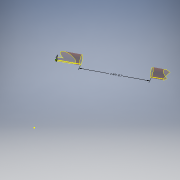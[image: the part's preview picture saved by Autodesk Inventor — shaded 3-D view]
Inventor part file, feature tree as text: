
AUTODESK INVENTOR PART (.ipt)
format: ipt  version: 2019.3 (Build 233278000, 278)  size: 225,280 bytes
history: native  units: mm
features: other x5, sketch x3, extrude x2, surface_op x2, plane x1, boolean_combine x1, delete_face x1
ambient origin geometry x8: Origin, YZ Plane, XZ Plane, XY Plane, X Axis, Y Axis, Z Axis, Center Point
bodies: Solid3 (feature_tree), Solid1 (feature_tree)
feature tree (15):
  other  "Swingarm.ipt"
  extrude  "Extrusion1"  Depth=10.0mm TaperAngle=0.0deg
  plane  "Work Plane2"
  extrude  "Extrusion2"  TaperAngle=0.0deg  [1 undecoded]
  boolean_combine  "Combine2"
  delete_face  "Delete Face2"
  sketch  "Sketch3"  dims[d9=0.0mm d10=0.0mm d11=0.0mm d12=1.0mm d13=3.0mm d18=149.665097mm]
  surface_op  "Trim1"
  surface_op  "Trim2"
  other  "Arms::Swingarm.ipt"
  other  "TaggingFeature2"
  sketch  "Sketch1"  dims[d1=10.0mm d2=52.5mm d3=0.0mm]
  sketch  "Sketch2"  dims[d6=35.75mm d7=0.0mm d8=0.0mm]
  other  "OffsetSrf2"
  other  "OffsetSrf3"
note: 1 required parameter value undecoded (feature->parameter linkage not recoverable at this tier; creation-order binding heuristic only, values carry confidence <= 0.55)
